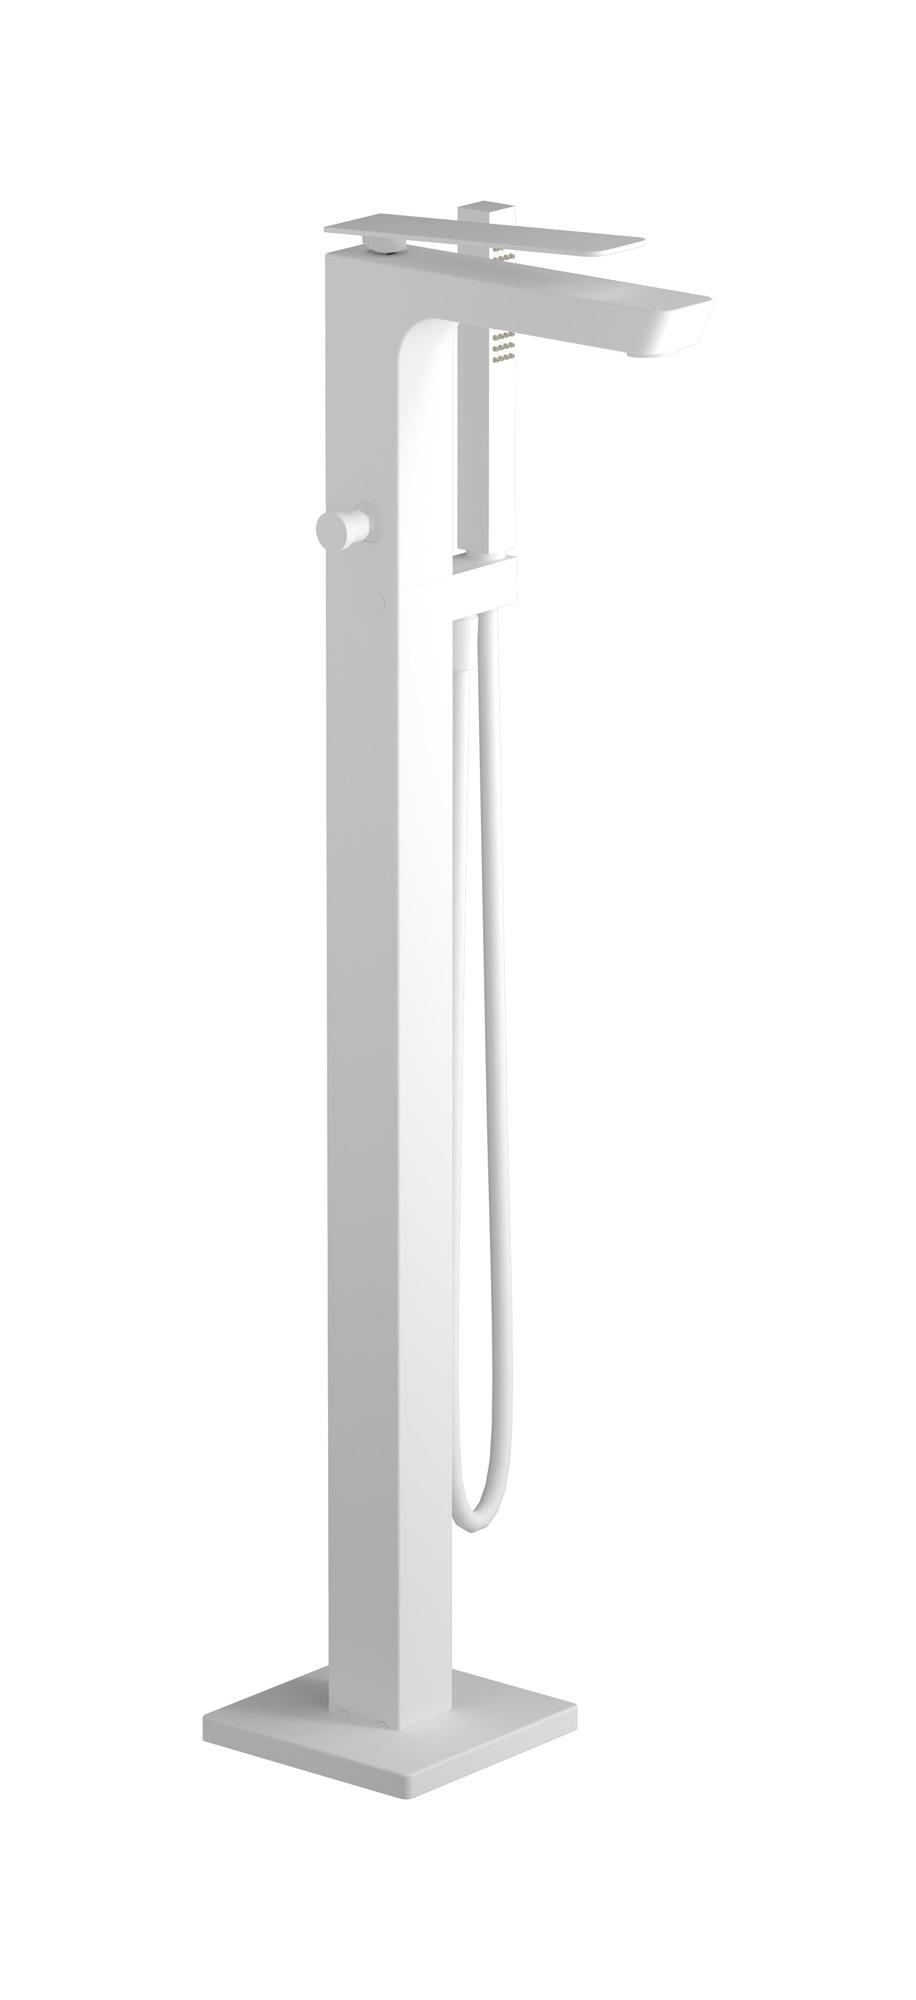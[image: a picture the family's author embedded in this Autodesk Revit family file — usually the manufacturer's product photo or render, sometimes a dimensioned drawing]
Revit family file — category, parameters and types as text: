
# Revit family: K3399
name_source: partatom
category: Apparecchi idraulici
units: mm (PartAtom-declared; Revit-internal decimal feet)

## family parameters
Basato su piano di lavoro = No
Condiviso = No
Mantieni orientamento annotazione = No
Numero OmniClass = 23.45.55.17
Punto di calcolo locali = No
Quota connettore circolare = Usa diametro
Sempre verticale = Sì
Taglio con vuoti quando caricato = No
Tipo di parte = Normale
Titolo OmniClass = Mixing Faucets

## types (8) — shared parameters
Cold water inlet = 10 mm  [stored 0.0328084 ft]
Commenti sul tipo = Bath filler
Connessione CW = No
Connessione HW = No
Connessione di scarico = No
Connessione di ventilazione = No
Descrizione = Freestanding bath filler
Hot water inlet = 10 mm  [stored 0.0328084 ft]
Produttore = IB Rubinetterie S.p.A.
URL = https://www.weareib.it
zero-valued in all types: Prospetto di default

## per-type parameters (varying)
| type | Finishes surface | Immagine tipo | Modello |
| Chrome | IB_Chrome | K3399CC.jpg | K3399CC |
| Brushed nickel | IB_Brushed nickel | K3399SS.jpg | K3399SS |
| Matt black | IB_matt black | K3399NP.jpg | K3399NP |
| Matt white | IB_matt white | K3399BO.jpg | K3399BO |
| Pale gold | IB_Pale gold | K3399II.jpg | K3399II |
| Brushed pale gold | IB_brushed pale gold | K3399IS.jpg | K3399IS |
| Rose gold | IB_Rose gold | K3399RS.jpg | K3399RS |
| Gold | IB_gold | K3399OO.jpg | K3399OO |

note: [stored X ft] marks values corroborated as IEEE doubles in the binary element streams (Revit-internal decimal feet)
